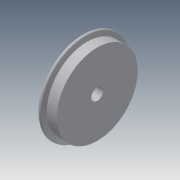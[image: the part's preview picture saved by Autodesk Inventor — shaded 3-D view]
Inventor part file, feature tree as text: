
AUTODESK INVENTOR PART (.ipt)
format: ipt  version: 2014 (Build 180170000, 170)  size: 117,248 bytes
history: native  units: in
note: dims shown in document units (in); Inventor stores cm internally (conversion verified against a paired STEP export)
features: sketch x2, revolve x1, extrude x1
ambient origin geometry x8: Origin, YZ Plane, XZ Plane, XY Plane, X Axis, Y Axis, Z Axis, Center Point
bodies: Solid1 (feature_tree)
feature tree (4):
  revolve  "Revolution1"  [1 undecoded]
  extrude  "Extrusion1"  Depth=1.0in
  sketch  "Sketch1"  dims[d0=1.0in d1=1.4375in]
  sketch  "Sketch2"  dims[d2=0.05in d3=0.46in d4=1.285in d5=0.14in d6=90.0deg d7=0.375in d8=1.0in d9=0.0in]
note: 1 required parameter value undecoded (feature->parameter linkage not recoverable at this tier; creation-order binding heuristic only, values carry confidence <= 0.55)
